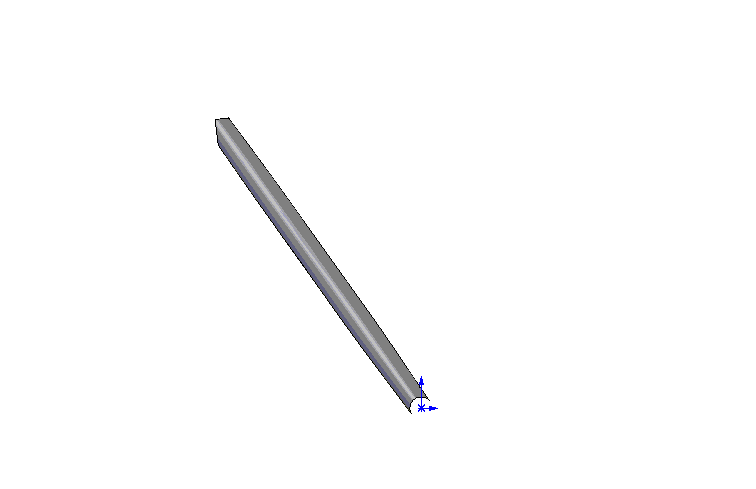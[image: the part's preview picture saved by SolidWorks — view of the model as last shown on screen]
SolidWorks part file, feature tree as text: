
SOLIDWORKS PART (.sldprt)
format: sldprt  version: not decoded by parser v0  size: 484,352 bytes
history: native  units: mm
features: plane x8, sketch x8, material x1, shell x1, cut_extrude x1, cut_revolve x1 (+10 scaffold rows collapsed)
feature tree (30):
  scaffold x10  (default folders/planes/origin — collapsed)
  material  "Matériau <non spécifié>"
  plane  "Plan de face"
  plane  "Plan de dessus"
  plane  "Plan de droite"
  sketch  "Esquisse1"  dims[c1.D1=625.0mm c1.D2=460.0mm c1.D3=545.0mm c1.D4=27.0mm c1.D5=500.0mm c1.D6=445.0mm c1.D7=670.0mm c2.D1=622.0mm c2.D2=670.0mm c2.D3=545.0mm c2.D4=460.0mm c2.D5=445.0mm c2.D6=495.0mm c2.D7=535.0mm c2.D8=27.0mm c2.D9=8.0mm c2.D10=155.0mm c2.D11=400.0mm c2.D12=~545.374305mm c3.D12=56.0deg]
  plane  "Plan1"
  plane  "Plan2"  Offset=180mm
  plane  "Plan3"  Offset=340mm
  plane  "Plan4"  Offset=500mm
  plane  "Plan5"
  sketch  "Esquisse5"  dims[c1.D1=42.0mm c1.D2=55.0mm c1.D3=2.0mm c1.D4=~8.95384mm c2.D3=2.0mm c2.D4=2.0mm]
  sketch  "Esquisse6"  dims[D1=50.0mm D2=46.0mm]
  sketch  "Esquisse7"  dims[D1=46.0mm]
  sketch  "Esquisse8"
  sketch  "Esquisse9"  dims[D1=45.0mm D2=41.0mm]
  shell  "Coque1"  Thickness=2mm
  sketch  "Esquisse2"  dims[D1=42.5mm]
  cut_extrude  "Enlèv. mat.-Extru.1"  [1 undecoded]
  sketch  "Esquisse3"  dims[c1.D1=50.0mm c1.D2=45.0mm c1.D3=~233.713088mm c2.D2=140.0mm c2.D3=45.0mm c2.D4=9.0mm c2.D5=80.0mm c2.D6=27.0mm]
  cut_revolve  "Enlèvement de matière-Révolution1"  Angle=360deg
decode coverage: 9 of 11 modeling features carry decoded parameters
note: ~ marks probable driven/reference dimensions
note: 1 parameter value undecoded
note: suppression state not decoded; provenance and decode notes live in map.json
